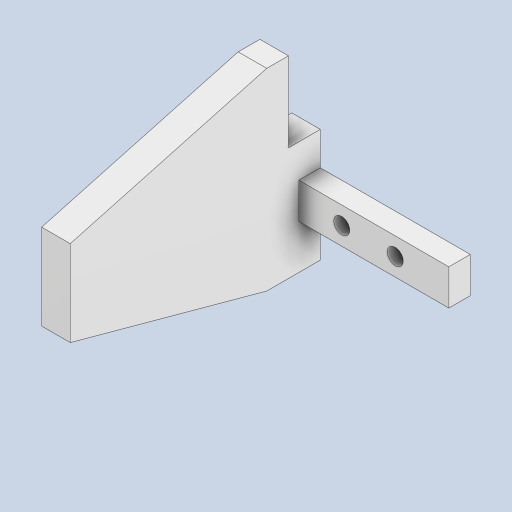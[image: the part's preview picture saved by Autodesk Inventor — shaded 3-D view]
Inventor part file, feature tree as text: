
AUTODESK INVENTOR PART (.ipt)
format: ipt  version: 2023 (Build 270158000, 158)  size: 146,432 bytes
history: native  units: in
note: dims shown in document units (in); Inventor stores cm internally (conversion verified against a paired STEP export)
features: extrude x4, sketch x3
ambient origin geometry x8: Origin, YZ Plane, XZ Plane, XY Plane, X Axis, Y Axis, Z Axis, Center Point
bodies: Body1 (feature_tree)
feature tree (7):
  sketch  "スケッチ2"
  extrude  "押し出し2"  Depth=1.9685in
  extrude  "押し出し5"  Depth=0.3937in
  extrude  "押し出し6"  Depth=0.315in
  extrude  "押し出し7"  Depth=0.1772in
  sketch  "スケッチ4"
  sketch  "スケッチ5"
